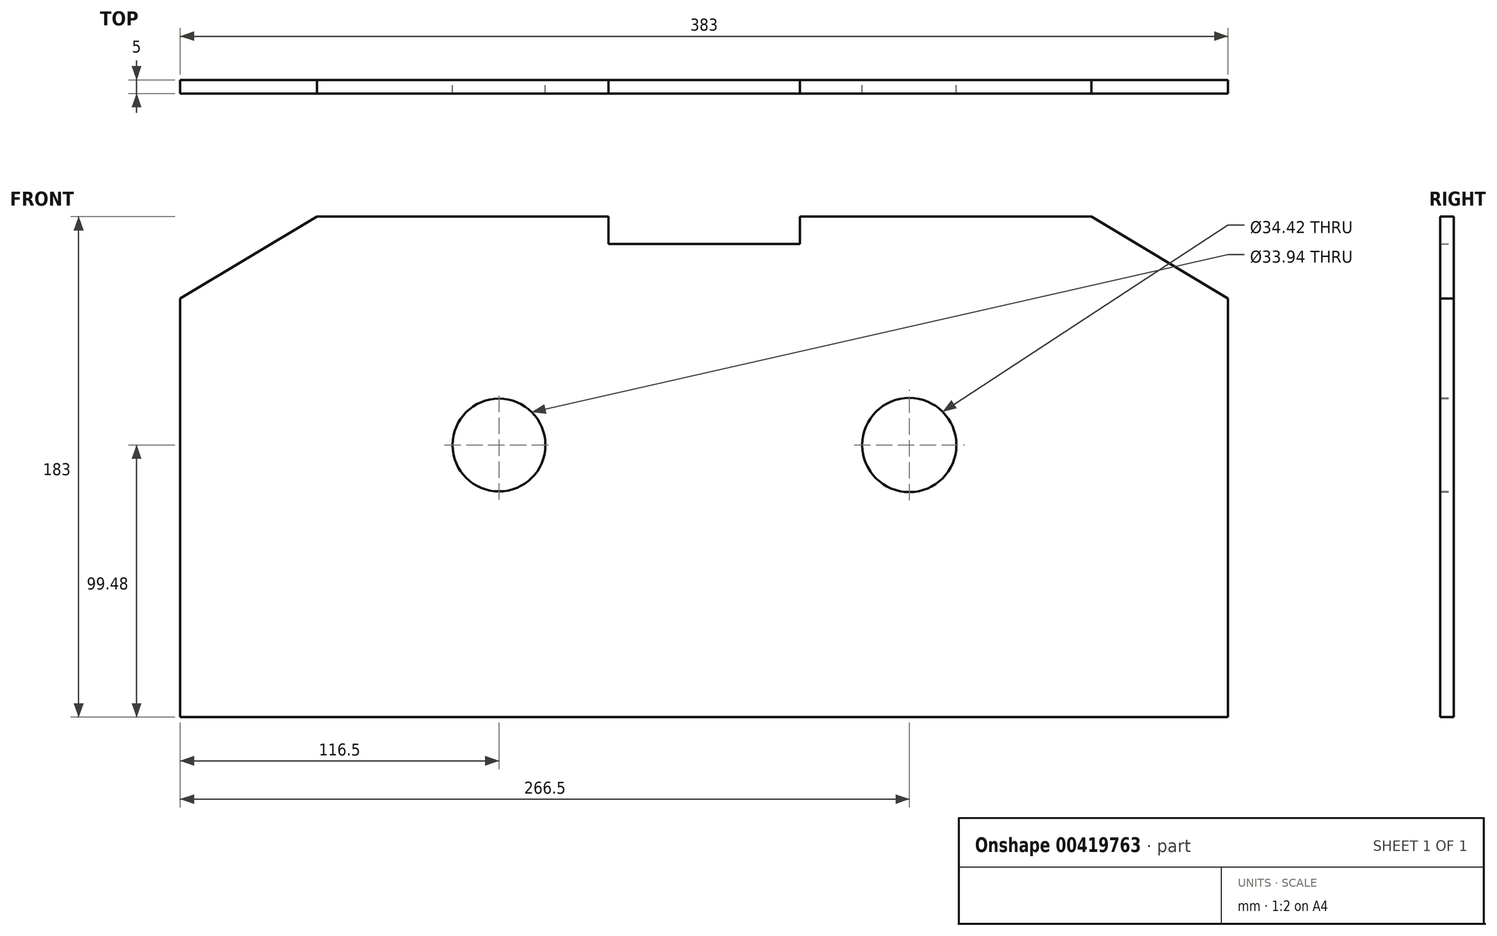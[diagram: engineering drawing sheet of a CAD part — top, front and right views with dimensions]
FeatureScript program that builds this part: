
annotation { "Feature Type Name" : "Feature", "Feature Type Description" : "" }
export const myFeature = defineFeature(function(context is Context, id is Id, definition is map)
    precondition{}
    {
        {
            var Q0;
            Q0=qCreatedBy(makeId("Front.planeOp"),FACE);
            var sketch = newSketch(context, id + "F0", { "sketchPlane" : qUnion([Q0])});
            skLineSegment(sketch, "E0.bottom", {"start": v(-191.5, 83.52) * mm, "end": v(191.5, 83.52) * mm});
            skLineSegment(sketch, "E0.top", {"start": v(-191.5, -99.48) * mm, "end": v(191.5, -99.48) * mm});
            skLineSegment(sketch, "E0.left", {"start": v(-191.5, 83.52) * mm, "end": v(-191.5, -99.48) * mm});
            skLineSegment(sketch, "E0.right", {"start": v(191.5, 83.52) * mm, "end": v(191.5, -99.48) * mm});
            skCircle(sketch, "E1", {"center": v(-75, 0) * mm, "radius": 16.97 * mm});
            skCircle(sketch, "E2", {"center": v(75, 0) * mm, "radius": 17.21 * mm});
            skLineSegment(sketch, "E3.bottom", {"start": v(-35, 83.52) * mm, "end": v(35, 83.52) * mm});
            skLineSegment(sketch, "E3.top", {"start": v(-35, 73.52) * mm, "end": v(35, 73.52) * mm});
            skLineSegment(sketch, "E3.left", {"start": v(-35, 83.52) * mm, "end": v(-35, 73.52) * mm});
            skLineSegment(sketch, "E3.right", {"start": v(35, 83.52) * mm, "end": v(35, 73.52) * mm});
            skLineSegment(sketch, "E4", {"start": v(141.5, 83.52) * mm, "end": v(191.5, 53.52) * mm});
            skLineSegment(sketch, "E5", {"start": v(-191.5, 53.52) * mm, "end": v(-141.5, 83.52) * mm});
            skSolve(sketch);
        }
        {
            var Q0;
            {var subQ2=sQuery(id+"F0.wireOp",EDGE,"E0.top");Q0=makeQuery(id+"F0.imprint","IMPRINT",FACE,{"disambiguationData":[TD([[makeQuery(id+"F0.imprint","IMPRINT",EDGE,{"derivedFrom":subQ2}),1.0]])]});}
            extrude(context, id + "F1", {"entities" : qUnion([Q0]), "depth" : 5 * mm});
        }
    });
